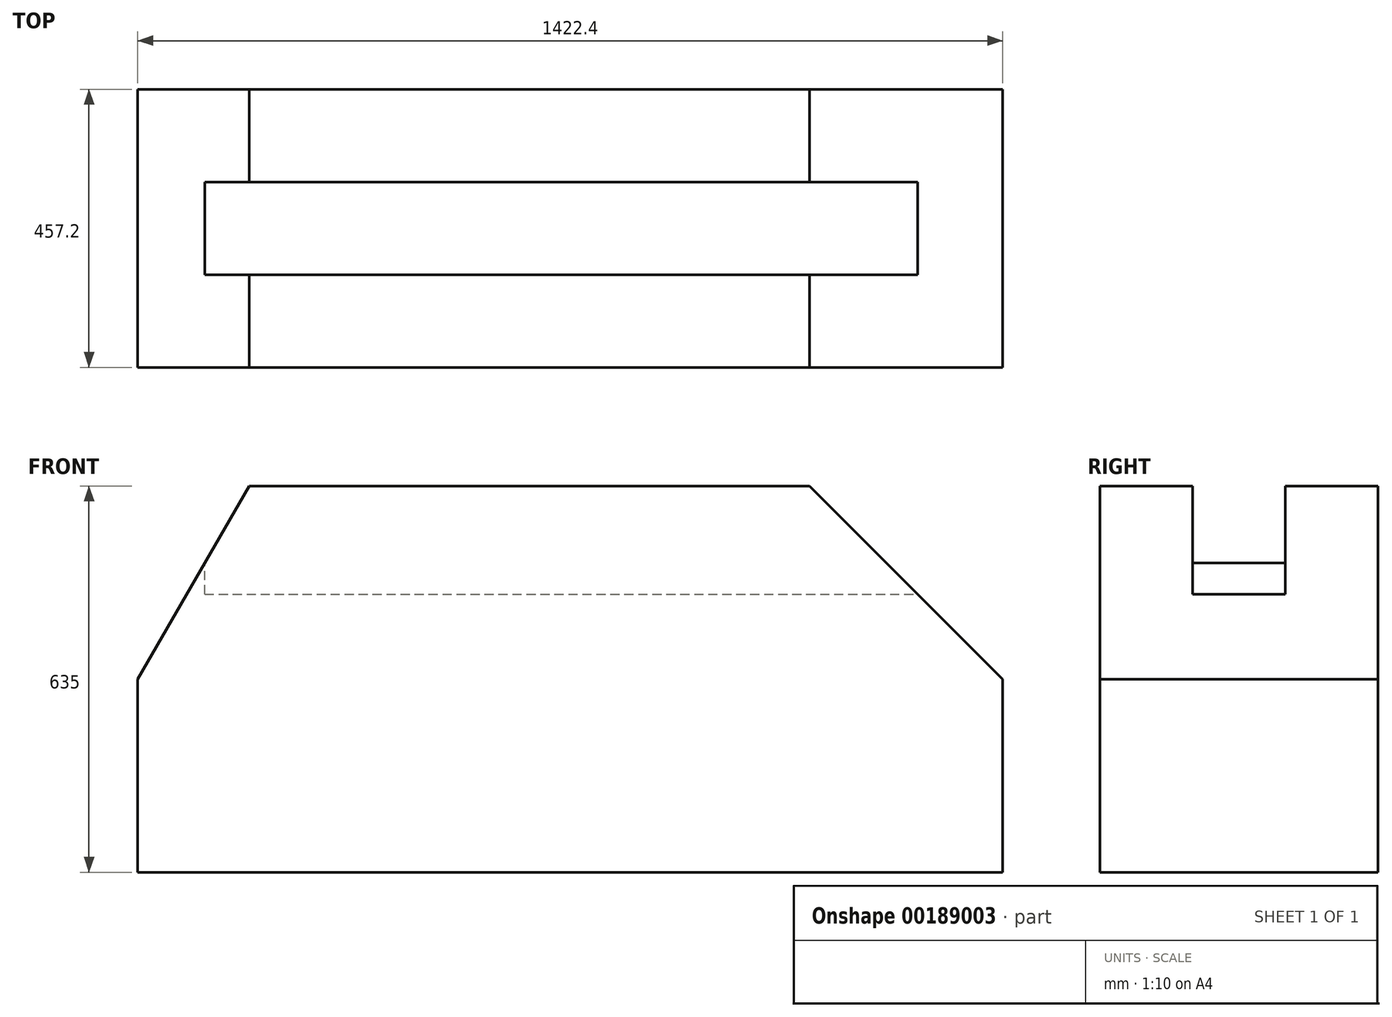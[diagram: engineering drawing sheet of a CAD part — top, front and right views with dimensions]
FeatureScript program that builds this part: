
annotation { "Feature Type Name" : "Feature", "Feature Type Description" : "" }
export const myFeature = defineFeature(function(context is Context, id is Id, definition is map)
    precondition{}
    {
        {
            var Q0;
            Q0=qCreatedBy(makeId("Front.planeOp"),FACE);
            var sketch = newSketch(context, id + "F0", { "sketchPlane" : qUnion([Q0])});
            skLineSegment(sketch, "E0.bottom", {"start": v(0, 0) * mm, "end": v(1422.4, 0) * mm});
            skLineSegment(sketch, "E0.top", {"start": v(0, 317.5) * mm, "end": v(1422.4, 317.5) * mm});
            skLineSegment(sketch, "E0.left", {"start": v(0, 0) * mm, "end": v(0, 317.5) * mm});
            skLineSegment(sketch, "E0.right", {"start": v(1422.4, 0) * mm, "end": v(1422.4, 317.5) * mm});
            skLineSegment(sketch, "E1", {"start": v(183.3, 635) * mm, "end": v(1104.9, 635) * mm});
            skLineSegment(sketch, "E2", {"start": v(0, 317.5) * mm, "end": v(183.3, 635) * mm});
            skLineSegment(sketch, "E3", {"start": v(1104.9, 635) * mm, "end": v(1422.4, 317.5) * mm});
            skSolve(sketch);
        }
        {
            var Q0;
            Q0=makeQuery(id+"F0.imprint","IMPRINT",FACE,{"disambiguationData":[TD([[makeQuery(id+"F0.imprint","IMPRINT",EDGE,{"derivedFrom":sQuery(id+"F0.wireOp",EDGE,"E0.bottom")}),1.0]])]});
            var Q1;
            Q1=makeQuery(id+"F0.imprint","IMPRINT",FACE,{"disambiguationData":[TD([[makeQuery(id+"F0.imprint","IMPRINT",EDGE,{"derivedFrom":sQuery(id+"F0.wireOp",EDGE,"E0.top")}),1.0]])]});
            extrude(context, id + "F1", {"entities" : qUnion([Q0, Q1]), "depth" : 457.2 * mm});
        }
        {
            var Q0;
            Q0=makeQuery(id+"F1.opExtrude","SWEPT_FACE",FACE,{"disambiguationData":[OSD([sQuery(id+"F0.wireOp",EDGE,"E1")])]});
            var sketch = newSketch(context, id + "F2", { "sketchPlane" : qUnion([Q0])});
            skLineSegment(sketch, "E4.bottom", {"start": v(110.24, -152.4) * mm, "end": v(1312.16, -152.4) * mm});
            skLineSegment(sketch, "E4.top", {"start": v(110.24, -304.8) * mm, "end": v(1312.16, -304.8) * mm});
            skLineSegment(sketch, "E4.left", {"start": v(110.24, -152.4) * mm, "end": v(110.24, -304.8) * mm});
            skLineSegment(sketch, "E4.right", {"start": v(1312.16, -152.4) * mm, "end": v(1312.16, -304.8) * mm});
            skPoint(sketch, "E4.middle", {"position": v(711.2, -228.6) * mm});
            skSolve(sketch);
        }
        {
            var Q0;
            {var subQ0=sQuery(id+"F2.wireOp",EDGE,"E4.left");Q0=makeQuery(id+"F2.imprint","IMPRINT",FACE,{"disambiguationData":[TD([[makeQuery(id+"F2.imprint","IMPRINT",EDGE,{"derivedFrom":subQ0}),1.0]])]});}
            var Q1;
            {var subQ0=sQuery(id+"F2.wireOp",EDGE,"E4.right");Q1=makeQuery(id+"F2.imprint","IMPRINT",FACE,{"disambiguationData":[TD([[makeQuery(id+"F2.imprint","IMPRINT",EDGE,{"derivedFrom":subQ0}),-1.0]])]});}
            var Q2;
            {var subQ0=sQuery(id+"F2.wireOp",EDGE,"E4.bottom");var subQ1=sQuery(id+"F0.wireOp",EDGE,"E1");var subQ2=makeQuery(id+"F1.opExtrude","SWEPT_EDGE",EDGE,{"disambiguationData":[OSD([subQ1,sQuery(id+"F0.wireOp",EDGE,"E2")])]});var subQ3=makeQuery(id+"F2.imprint","INTERSECT",VERTEX,{"derivedFrom":[subQ2,subQ0]});Q2=makeQuery(id+"F2.imprint","IMPRINT",FACE,{"disambiguationData":[TD([[makeQuery(id+"F2.imprint","IMPRINT",EDGE,{"disambiguationData":[TD([[subQ3,-1.0]])],"derivedFrom":subQ0}),-1.0]])]});}
            extrude(context, id + "F3", {"entities" : qUnion([Q0, Q1, Q2]), "operationType" : NewBodyOperationType.REMOVE, "oppositeDirection" : true, "depth" : 177.8 * mm});
        }
    });
